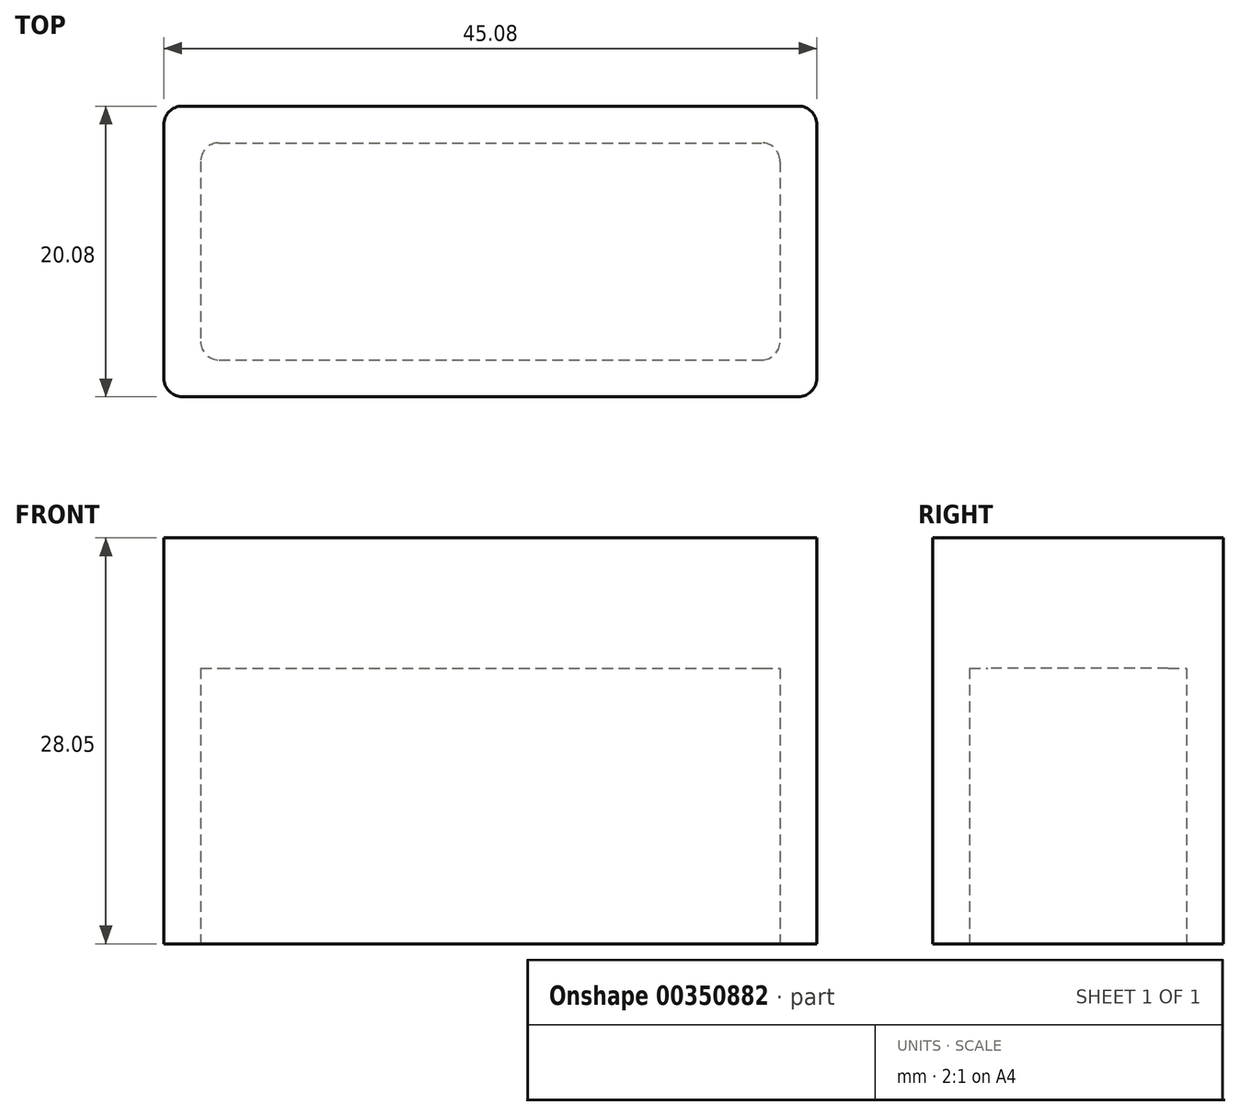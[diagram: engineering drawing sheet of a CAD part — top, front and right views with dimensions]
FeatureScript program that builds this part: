
annotation { "Feature Type Name" : "Feature", "Feature Type Description" : "" }
export const myFeature = defineFeature(function(context is Context, id is Id, definition is map)
    precondition{}
    {
        {
            var Q0;
            Q0=qCreatedBy(makeId("Top.planeOp"),FACE);
            var sketch = newSketch(context, id + "F0", { "sketchPlane" : qUnion([Q0])});
            skLineSegment(sketch, "E0.bottom", {"start": v(-20, 7.5) * mm, "end": v(20, 7.5) * mm});
            skLineSegment(sketch, "E0.top", {"start": v(-20, -7.5) * mm, "end": v(20, -7.5) * mm});
            skLineSegment(sketch, "E0.left", {"start": v(-20, 7.5) * mm, "end": v(-20, -7.5) * mm});
            skLineSegment(sketch, "E0.right", {"start": v(20, 7.5) * mm, "end": v(20, -7.5) * mm});
            skPoint(sketch, "E0.middle", {"position": v(0, 0) * mm});
            skLineSegment(sketch, "E1.bottom", {"start": v(-22.54, 10.04) * mm, "end": v(22.54, 10.04) * mm});
            skLineSegment(sketch, "E1.top", {"start": v(-22.54, -10.04) * mm, "end": v(22.54, -10.04) * mm});
            skLineSegment(sketch, "E1.left", {"start": v(-22.54, 10.04) * mm, "end": v(-22.54, -10.04) * mm});
            skLineSegment(sketch, "E1.right", {"start": v(22.54, 10.04) * mm, "end": v(22.54, -10.04) * mm});
            skSolve(sketch);
        }
        {
            var Q0;
            Q0 = qSketchRegion(id + "F0", true);
            extrude(context, id + "F1", {"entities" : qUnion([Q0]), "depth" : 19.05 * mm});
        }
        {
            var Q0;
            Q0=makeQuery(id+"F1.opExtrude","SWEPT_EDGE",EDGE,{"disambiguationData":[OSD([sQuery(id+"F0.wireOp",EDGE,"E0.bottom"),sQuery(id+"F0.wireOp",EDGE,"E0.left")])]});
            var Q1;
            Q1=makeQuery(id+"F1.opExtrude","SWEPT_EDGE",EDGE,{"disambiguationData":[OSD([sQuery(id+"F0.wireOp",EDGE,"E0.top"),sQuery(id+"F0.wireOp",EDGE,"E0.left")])]});
            var Q2;
            Q2=makeQuery(id+"F1.opExtrude","SWEPT_EDGE",EDGE,{"disambiguationData":[OSD([sQuery(id+"F0.wireOp",EDGE,"E0.bottom"),sQuery(id+"F0.wireOp",EDGE,"E0.right")])]});
            var Q3;
            Q3=makeQuery(id+"F1.opExtrude","SWEPT_EDGE",EDGE,{"disambiguationData":[OSD([sQuery(id+"F0.wireOp",EDGE,"E0.top"),sQuery(id+"F0.wireOp",EDGE,"E0.right")])]});
            var Q4;
            Q4=makeQuery(id+"F1.opExtrude","SWEPT_EDGE",EDGE,{"disambiguationData":[OSD([sQuery(id+"F0.wireOp",EDGE,"E1.top"),sQuery(id+"F0.wireOp",EDGE,"E1.left")])]});
            var Q5;
            Q5=makeQuery(id+"F1.opExtrude","SWEPT_EDGE",EDGE,{"disambiguationData":[OSD([sQuery(id+"F0.wireOp",EDGE,"E1.bottom"),sQuery(id+"F0.wireOp",EDGE,"E1.left")])]});
            var Q6;
            Q6=makeQuery(id+"F1.opExtrude","SWEPT_EDGE",EDGE,{"disambiguationData":[OSD([sQuery(id+"F0.wireOp",EDGE,"E1.top"),sQuery(id+"F0.wireOp",EDGE,"E1.right")])]});
            var Q7;
            Q7=makeQuery(id+"F1.opExtrude","SWEPT_EDGE",EDGE,{"disambiguationData":[OSD([sQuery(id+"F0.wireOp",EDGE,"E1.bottom"),sQuery(id+"F0.wireOp",EDGE,"E1.right")])]});
            fillet(context, id + "F2", {"entities" : qUnion([Q0, Q1, Q2, Q3, Q4, Q5, Q6, Q7]), "radius" : 1.27 * mm, "tangentPropagation" : true, "allowEdgeOverflow" : false});
        }
        {
            var Q0;
            Q0=makeQuery(id+"F1.opExtrude","CAP_FACE",FACE,{"disambiguationData":[OSD([sQuery(id+"F0.wireOp",EDGE,"E0.bottom"),sQuery(id+"F0.wireOp",EDGE,"E0.top"),sQuery(id+"F0.wireOp",EDGE,"E0.left"),sQuery(id+"F0.wireOp",EDGE,"E0.right"),sQuery(id+"F0.wireOp",EDGE,"E1.bottom"),sQuery(id+"F0.wireOp",EDGE,"E1.top"),sQuery(id+"F0.wireOp",EDGE,"E1.left"),sQuery(id+"F0.wireOp",EDGE,"E1.right")])],"isStart":false});
            var sketch = newSketch(context, id + "F3", { "sketchPlane" : qUnion([Q0])});
            skLineSegment(sketch, "E2.0", {"start": v(-21.27, 10.04) * mm, "end": v(21.27, 10.04) * mm});
            skLineSegment(sketch, "E3.0", {"start": v(-22.54, 8.77) * mm, "end": v(-22.54, -8.77) * mm});
            skLineSegment(sketch, "E4.0", {"start": v(-21.27, -10.04) * mm, "end": v(21.27, -10.04) * mm});
            skLineSegment(sketch, "E5.0", {"start": v(22.54, 8.77) * mm, "end": v(22.54, -8.77) * mm});
            skArc(sketch, "E6.0", {"start": v(22.54, 8.77) * mm, "mid": v(22.17, 9.67) * mm, "end": v(21.27, 10.04) * mm});
            skArc(sketch, "E7.0", {"start": v(-21.27, 10.04) * mm, "mid": v(-22.17, 9.67) * mm, "end": v(-22.54, 8.77) * mm});
            skArc(sketch, "E8.0", {"start": v(-22.54, -8.77) * mm, "mid": v(-22.17, -9.67) * mm, "end": v(-21.27, -10.04) * mm});
            skArc(sketch, "E9.0", {"start": v(21.27, -10.04) * mm, "mid": v(22.17, -9.67) * mm, "end": v(22.54, -8.77) * mm});
            skSolve(sketch);
        }
        {
            var Q0;
            Q0 = qSketchRegion(id + "F3", true);
            extrude(context, id + "F4", {"entities" : qUnion([Q0]), "operationType" : NewBodyOperationType.ADD, "depth" : 9 * mm});
        }
    });
